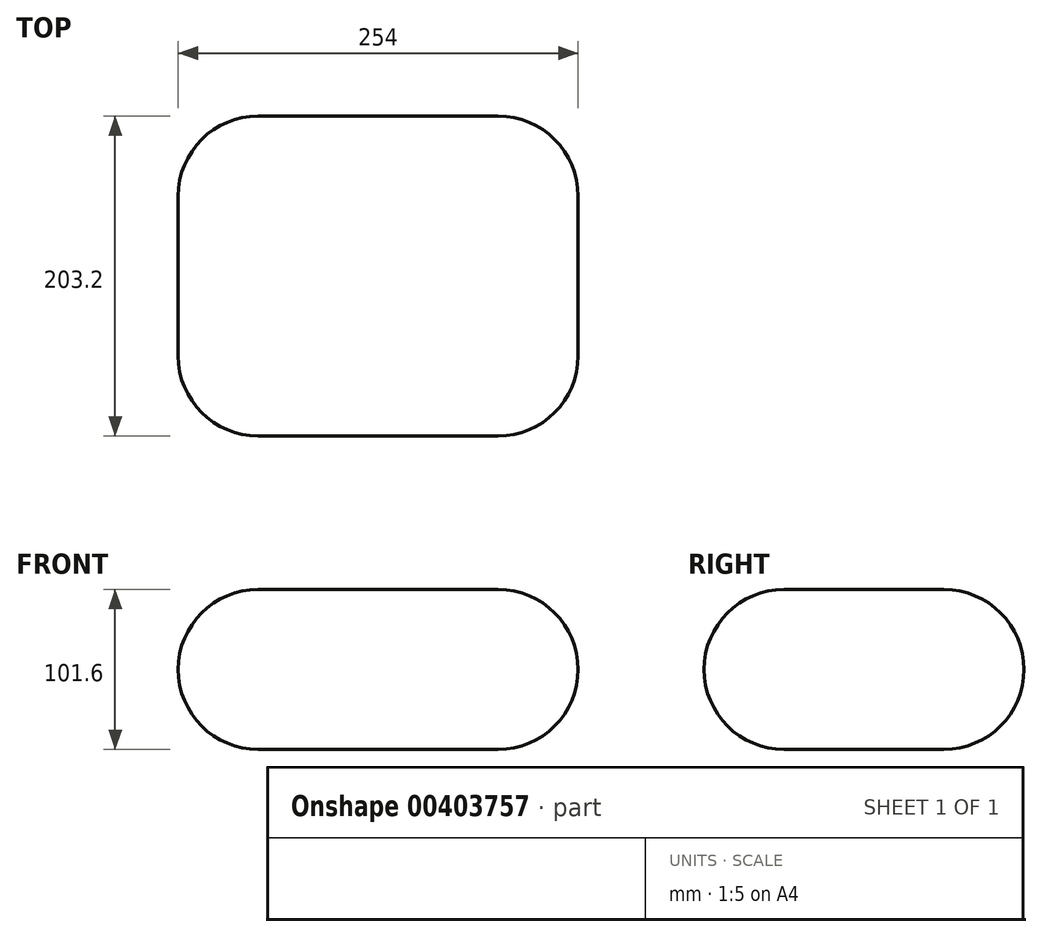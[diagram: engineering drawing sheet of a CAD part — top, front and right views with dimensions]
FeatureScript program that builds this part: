
annotation { "Feature Type Name" : "Feature", "Feature Type Description" : "" }
export const myFeature = defineFeature(function(context is Context, id is Id, definition is map)
    precondition{}
    {
        {
            var Q0;
            Q0=qCreatedBy(makeId("Top.planeOp"),FACE);
            var sketch = newSketch(context, id + "F0", { "sketchPlane" : qUnion([Q0])});
            skLineSegment(sketch, "E0.bottom", {"start": v(-127, 101.6) * mm, "end": v(127, 101.6) * mm});
            skLineSegment(sketch, "E0.top", {"start": v(-127, -101.6) * mm, "end": v(127, -101.6) * mm});
            skLineSegment(sketch, "E0.left", {"start": v(-127, 101.6) * mm, "end": v(-127, -101.6) * mm});
            skLineSegment(sketch, "E0.right", {"start": v(127, 101.6) * mm, "end": v(127, -101.6) * mm});
            skPoint(sketch, "E0.middle", {"position": v(0, 0) * mm});
            skSolve(sketch);
        }
        {
            var Q0;
            Q0 = qSketchRegion(id + "F0", true);
            extrude(context, id + "F1", {"entities" : qUnion([Q0]), "depth" : 101.6 * mm});
        }
        {
            var Q0;
            Q0=makeQuery(id+"F1.opExtrude","SWEPT_FACE",FACE,{"disambiguationData":[OSD([sQuery(id+"F0.wireOp",EDGE,"E0.top")])]});
            var Q1;
            Q1=makeQuery(id+"F1.opExtrude","SWEPT_FACE",FACE,{"disambiguationData":[OSD([sQuery(id+"F0.wireOp",EDGE,"E0.right")])]});
            var Q2;
            Q2=makeQuery(id+"F1.opExtrude","SWEPT_FACE",FACE,{"disambiguationData":[OSD([sQuery(id+"F0.wireOp",EDGE,"E0.bottom")])]});
            var Q3;
            Q3=makeQuery(id+"F1.opExtrude","SWEPT_FACE",FACE,{"disambiguationData":[OSD([sQuery(id+"F0.wireOp",EDGE,"E0.left")])]});
            fillet(context, id + "F2", {"entities" : qUnion([Q0, Q1, Q2, Q3]), "radius" : 50.8 * mm, "tangentPropagation" : true, "allowEdgeOverflow" : false});
        }
    });
